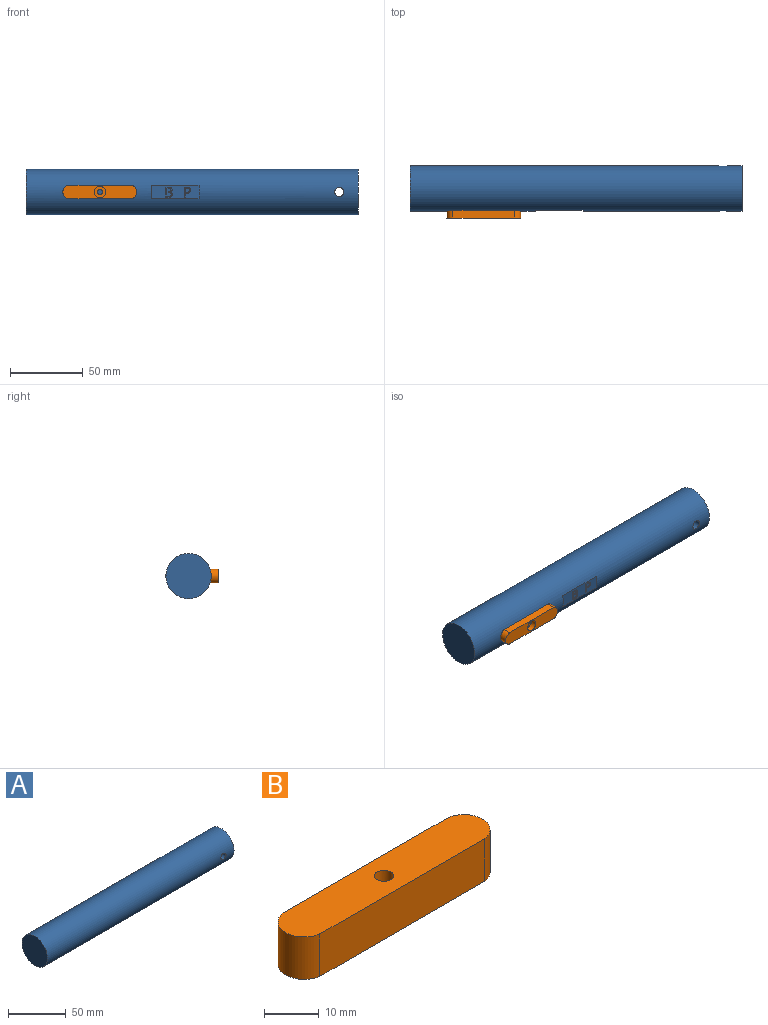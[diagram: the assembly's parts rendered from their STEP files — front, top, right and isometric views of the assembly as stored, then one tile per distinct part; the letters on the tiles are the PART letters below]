
ASSEMBLY  parts=2 mates=1
PART A: 62 faces, bbox 228.6x31.2x31.2 mm
  f0: plane 32.77x9.39mm, normal (0,1,0), area 260.6mm2, adj f1,f13,f14,f27,f28,f29,f30,f31
  f1: cylinder r=15.58mm len=228.6mm, axis (-1,0,0), area 21536.6mm2, adj f0,f2,f3,f4,f5,f6,f7,f13
  f2: plane 31.17x31.17mm, normal (1,0,0), area 477.8mm2, adj f1,f11
  f3: plane 31.17x31.17mm, normal (-1,0,0), area 762.9mm2, adj f1
  f4: plane 42.57x4.05mm, normal (0,0,-1), area 172.4mm2, adj f1,f5,f7,f8
  f5: cylinder r=4.78mm len=9.47mm, axis (0,1,0), area 60.9mm2, adj f1,f4,f6,f8
  f6: plane 42.57x4.05mm, normal (0,0,1), area 172.4mm2, adj f1,f5,f7,f8
  f7: cylinder r=4.78mm len=9.47mm, axis (0,1,0), area 60.9mm2, adj f1,f4,f6,f8
  f8: plane 50.8x9.47mm, normal (0,1,0), area 453.1mm2, adj f4,f5,f6,f7,f9
  f9: cylinder r=1.73mm len=19.05mm, axis (0,1,0), area 206.7mm2, adj f8,f10
  f10: plane 3.45x3.45mm, normal (0,1,0), area 9.4mm2, adj f9
  f11: cylinder r=9.53mm len=50.8mm, axis (1,0,0), area 2976.1mm2, adj f2,f12,f60,f61
  f12: plane 19.05x19.05mm, normal (1,0,0), area 285mm2, adj f11
  f13: plane 9.39x0.72mm, normal (-1,0,0), area 4.6mm2, adj f0,f1
  f14: plane 9.39x0.72mm, normal (1,0,0), area 4.6mm2, adj f0,f1
  f15: plane 2.52x0.25mm, normal (-1,0,0), area 0.6mm2, adj f16,f39,f40,f58
  f16: plane 1.34x0.25mm, normal (0,0,-1), area 0.3mm2, adj f15,f17,f40,f58
  f17: extruded ~1.28x0.29mm, area 0.3mm2, adj f16,f18,f40,f58
  f18: extruded ~0.92x0.42mm, area 0.3mm2, adj f17,f19,f40,f58
  f19: extruded ~0.99x0.41mm, area 0.3mm2, adj f18,f20,f40,f58
  f20: extruded ~1.23x0.32mm, area 0.3mm2, adj f19,f39,f40,f58
  f21: plane 1.29x0.25mm, normal (0,0,1), area 0.3mm2, adj f22,f37,f40,f41
  f22: plane 2.2x0.25mm, normal (-1,0,0), area 0.6mm2, adj f21,f23,f40,f41
  f23: plane 1.15x0.25mm, normal (0,0,-1), area 0.3mm2, adj f22,f24,f40,f41
  f24: extruded ~1.29x0.25mm, area 0.3mm2, adj f23,f25,f40,f41
  f25: extruded ~0.82x0.4mm, area 0.2mm2, adj f24,f26,f40,f41
  f26: extruded ~0.88x0.36mm, area 0.3mm2, adj f25,f37,f40,f41
  f27: plane 1.9x0.25mm, normal (0,0,1), area 0.5mm2, adj f0,f28,f38,f40
  f28: plane 6.72x0.25mm, normal (1,0,0), area 1.7mm2, adj f0,f27,f29,f40
  f29: plane 2.35x0.25mm, normal (0,0,-1), area 0.6mm2, adj f0,f28,f30,f40
  f30: extruded ~1.7x0.51mm, area 0.5mm2, adj f0,f29,f31,f40
  f31: extruded ~1.41x0.61mm, area 0.4mm2, adj f0,f30,f32,f40
  f32: extruded ~1.61x1.53mm, area 0.6mm2, adj f0,f31,f33,f40
  f33: plane 0.25x0.05mm, normal (-1,0,0), area 0mm2, adj f0,f32,f34,f40
  f34: extruded ~0.97x0.5mm, area 0.3mm2, adj f0,f33,f35,f40
  f35: extruded ~0.99x0.33mm, area 0.3mm2, adj f0,f34,f36,f40
  f36: extruded ~1.26x0.6mm, area 0.4mm2, adj f0,f35,f38,f40
  f37: extruded ~1.19x0.26mm, area 0.3mm2, adj f21,f26,f40,f41
  f38: extruded ~1.94x0.4mm, area 0.5mm2, adj f0,f27,f36,f40
  f39: plane 1.4x0.25mm, normal (0,0,1), area 0.4mm2, adj f15,f20,f40,f58
  f40: plane 6.72x4.66mm, normal (0,1,0), area 15.4mm2, adj f15,f16,f17,f18,f19,f20,f21,f22
  f41: plane 2.84x2.2mm, normal (0,1,0), area 5.7mm2, adj f21,f22,f23,f24,f25,f26,f37
  f42: plane 0.73x0.25mm, normal (0,0,1), area 0.2mm2, adj f43,f56,f57,f59
  f43: plane 2.83x0.25mm, normal (-1,0,0), area 0.7mm2, adj f42,f44,f57,f59
  f44: plane 0.91x0.25mm, normal (0,0,-1), area 0.2mm2, adj f43,f45,f57,f59
  f45: extruded ~1.41x0.34mm, area 0.4mm2, adj f44,f46,f57,f59
  f46: extruded ~1.03x0.45mm, area 0.3mm2, adj f45,f47,f57,f59
  f47: extruded ~1.12x0.48mm, area 0.3mm2, adj f46,f56,f57,f59
  f48: extruded ~1.63x0.72mm, area 0.5mm2, adj f0,f49,f55,f57
  f49: extruded ~2.61x2.03mm, area 1mm2, adj f0,f48,f50,f57
  f50: plane 1.81x0.25mm, normal (0,0,1), area 0.5mm2, adj f0,f49,f51,f57
  f51: plane 6.97x0.25mm, normal (1,0,0), area 1.8mm2, adj f0,f50,f52,f57
  f52: plane 0.81x0.25mm, normal (0,0,-1), area 0.2mm2, adj f0,f51,f53,f57
  f53: plane 2.74x0.25mm, normal (-1,0,0), area 0.7mm2, adj f0,f52,f54,f57
  f54: plane 0.82x0.25mm, normal (0,0,-1), area 0.2mm2, adj f0,f53,f55,f57
  f55: extruded ~2.07x0.57mm, area 0.6mm2, adj f0,f48,f54,f57
  f56: extruded ~1.56x0.35mm, area 0.4mm2, adj f42,f47,f57,f59
  f57: plane 6.97x4.42mm, normal (0,1,0), area 12mm2, adj f42,f43,f44,f45,f46,f47,f48,f49
  f58: plane 3.04x2.52mm, normal (0,1,0), area 7mm2, adj f15,f16,f17,f18,f19,f20,f39
  f59: plane 2.83x2.77mm, normal (0,1,0), area 7mm2, adj f42,f43,f44,f45,f46,f47,f56
  f60: cylinder r=3.17mm len=6.6mm, axis (0,-1,0), area 123mm2, adj f1,f11
  f61: cylinder r=3.17mm len=6.6mm, axis (0,-1,0), area 123mm2, adj f1,f11
PART B: 9 faces, bbox 50.8x9.5x9.5 mm
  f0: plane 42.57x9.49mm, normal (0,1,0), area 403.8mm2, adj f1,f3,f4,f5
  f1: cylinder r=4.78mm len=9.49mm, axis (0,0,-1), area 129.9mm2, adj f0,f2,f4,f5
  f2: plane 42.57x9.49mm, normal (0,-1,0), area 403.8mm2, adj f1,f3,f4,f5
  f3: cylinder r=4.78mm len=9.49mm, axis (0,0,-1), area 129.9mm2, adj f0,f2,f4,f5
  f4: plane 50.8x9.47mm, normal (0,0,1), area 453.1mm2, adj f0,f1,f2,f3,f6
  f5: plane 50.8x9.47mm, normal (0,0,-1), area 413mm2, adj f0,f1,f2,f3,f8
  f6: cylinder r=1.73mm len=5.32mm, axis (0,0,-1), area 57.7mm2, adj f4,f7
  f7: plane 7.94x7.94mm, normal (0,0,-1), area 40.1mm2, adj f6,f8
  f8: cylinder r=3.97mm len=7.94mm, axis (0,0,-1), area 103.9mm2, adj f5,f7
PLACE A rot(axis=(-1,0,0),180deg) t=(-38.74,26.81,-5.87)mm
PLACE B rot(axis=(-1,0,0),90deg) t=(12.06,6.53,-5.87)mm
MATE fastened B.f3 <-> A.f7  axis (0,1,0) through (32.68,16.02,-5.87)mm
